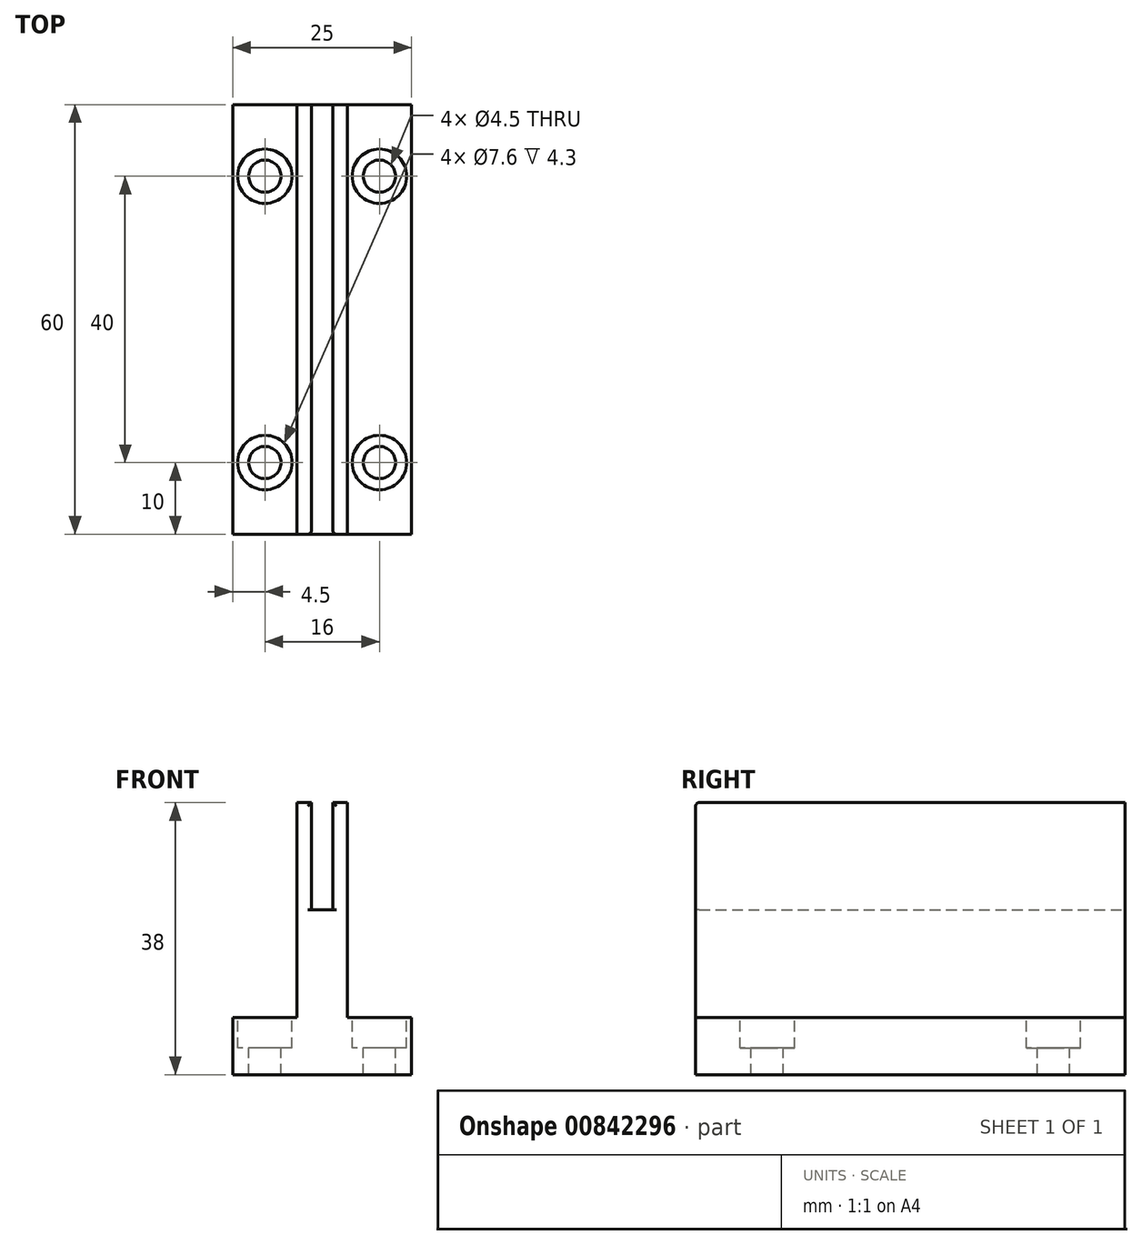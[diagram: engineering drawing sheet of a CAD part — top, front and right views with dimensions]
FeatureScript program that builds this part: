
annotation { "Feature Type Name" : "Feature", "Feature Type Description" : "" }
export const myFeature = defineFeature(function(context is Context, id is Id, definition is map)
    precondition{}
    {
        {
            var Q0;
            Q0=qCreatedBy(makeId("Front.planeOp"),FACE);
            var sketch = newSketch(context, id + "F0", { "sketchPlane" : qUnion([Q0])});
            skLineSegment(sketch, "E0", {"start": v(0, 17.87) * mm, "end": v(-1.5, 17.87) * mm});
            skLineSegment(sketch, "E1", {"start": v(-1.5, 17.87) * mm, "end": v(-1.5, 32.87) * mm});
            skLineSegment(sketch, "E2", {"start": v(-1.5, 32.87) * mm, "end": v(-3.5, 32.87) * mm});
            skLineSegment(sketch, "E3", {"start": v(-3.5, 32.87) * mm, "end": v(-3.5, 2.87) * mm});
            skLineSegment(sketch, "E4", {"start": v(-3.5, 2.87) * mm, "end": v(-12.5, 2.87) * mm});
            skLineSegment(sketch, "E5", {"start": v(-12.5, 2.87) * mm, "end": v(-12.5, -5.13) * mm});
            skLineSegment(sketch, "E6", {"start": v(-12.5, -5.13) * mm, "end": v(0, -5.13) * mm});
            skLineSegment(sketch, "E7", {"start": v(0, -5.13) * mm, "end": v(0, 17.87) * mm});
            skLineSegment(sketch, "E8.MirrorCS", {"start": v(1.5, 32.87) * mm, "end": v(3.5, 32.87) * mm});
            skLineSegment(sketch, "E9.MirrorCS", {"start": v(3.5, 32.87) * mm, "end": v(3.5, 2.87) * mm});
            skLineSegment(sketch, "E10.MirrorCS", {"start": v(3.5, 2.87) * mm, "end": v(12.5, 2.87) * mm});
            skLineSegment(sketch, "E11.MirrorCS", {"start": v(1.5, 17.87) * mm, "end": v(1.5, 32.87) * mm});
            skLineSegment(sketch, "E12.MirrorCS", {"start": v(12.5, 2.87) * mm, "end": v(12.5, -5.13) * mm});
            skLineSegment(sketch, "E13.MirrorCS", {"start": v(12.5, -5.13) * mm, "end": v(0, -5.13) * mm});
            skLineSegment(sketch, "E14.MirrorCS", {"start": v(0, 17.87) * mm, "end": v(1.5, 17.87) * mm});
            skSolve(sketch);
        }
        {
            var Q0;
            Q0=makeQuery(id+"F0.imprint","IMPRINT",FACE,{"disambiguationData":[TD([[makeQuery(id+"F0.imprint","IMPRINT",EDGE,{"derivedFrom":sQuery(id+"F0.wireOp",EDGE,"E0")}),1.0]])]});
            var Q1;
            Q1=makeQuery(id+"F0.imprint","IMPRINT",FACE,{"disambiguationData":[TD([[makeQuery(id+"F0.imprint","IMPRINT",EDGE,{"derivedFrom":sQuery(id+"F0.wireOp",EDGE,"E7")}),-1.0]])]});
            extrude(context, id + "F1", {"entities" : qUnion([Q0, Q1]), "depth" : 60 * mm, "offsetDistance" : 25 * mm});
        }
        {
            var Q0;
            Q0=makeQuery(id+"F1.opExtrude","SWEPT_FACE",FACE,{"disambiguationData":[OSD([sQuery(id+"F0.wireOp",EDGE,"E10.MirrorCS")])]});
            var sketch = newSketch(context, id + "F2", { "sketchPlane" : qUnion([Q0])});
            skCircle(sketch, "E15", {"center": v(8, -50) * mm, "radius": 1.96 * mm});
            skCircle(sketch, "E16", {"center": v(8, -50) * mm, "radius": 1.9 * mm});
            skCircle(sketch, "E17", {"center": v(8, -10) * mm, "radius": 2.01 * mm});
            skCircle(sketch, "E18", {"center": v(-8, -50) * mm, "radius": 2.05 * mm});
            skCircle(sketch, "E19", {"center": v(-8, -10) * mm, "radius": 2.04 * mm});
            skSolve(sketch);
        }
        {
            var Q0;
            Q0=sQuery(id+"F2.wireOp",VERTEX,"E18.center");
            var Q1;
            Q1=sQuery(id+"F2.wireOp",VERTEX,"E19.center");
            var Q2;
            Q2=sQuery(id+"F2.wireOp",VERTEX,"E15.center");
            var Q3;
            Q3=sQuery(id+"F2.wireOp",VERTEX,"E17.center");
            var Q4;
            Q4=makeQuery(id+"F1.opExtrude","SWEPT_BODY",BODY,{"disambiguationData":[OSD([sQuery(id+"F0.wireOp",EDGE,"E0"),sQuery(id+"F0.wireOp",EDGE,"E1"),sQuery(id+"F0.wireOp",EDGE,"E2"),sQuery(id+"F0.wireOp",EDGE,"E3"),sQuery(id+"F0.wireOp",EDGE,"E4"),sQuery(id+"F0.wireOp",EDGE,"E5"),sQuery(id+"F0.wireOp",EDGE,"E6"),sQuery(id+"F0.wireOp",EDGE,"E8.MirrorCS"),sQuery(id+"F0.wireOp",EDGE,"E9.MirrorCS"),sQuery(id+"F0.wireOp",EDGE,"E10.MirrorCS"),sQuery(id+"F0.wireOp",EDGE,"E11.MirrorCS"),sQuery(id+"F0.wireOp",EDGE,"E12.MirrorCS"),sQuery(id+"F0.wireOp",EDGE,"E13.MirrorCS"),sQuery(id+"F0.wireOp",EDGE,"E14.MirrorCS")])]});
            hole(context, id + "F3", {"style" : HoleStyle.C_BORE, "endStyle" : HoleEndStyle.THROUGH, "holeDiameter" : 4.5 * mm, "cBoreDiameter" : 7.6 * mm, "cBoreDepth" : 4.3 * mm, "majorDiameter" : 5 * mm, "isTappedThrough" : true, "tappedDepth" : 12 * mm, "tapClearance" : 3, "startFromSketch" : true, "locations" : qUnion([Q0, Q1, Q2, Q3]), "scope" : qUnion([Q4])});
        }
        {
            var Q0;
            Q0=makeQuery(id+"F1.opExtrude","CAP_EDGE",EDGE,{"disambiguationData":[OSD([sQuery(id+"F0.wireOp",EDGE,"E1")])],"isStart":false});
            var Q1;
            Q1=makeQuery(id+"F1.opExtrude","CAP_EDGE",EDGE,{"disambiguationData":[OSD([sQuery(id+"F0.wireOp",EDGE,"E11.MirrorCS")])],"isStart":false});
            var Q2;
            Q2=makeQuery(id+"F1.opExtrude","CAP_EDGE",EDGE,{"disambiguationData":[OSD([sQuery(id+"F0.wireOp",EDGE,"E8.MirrorCS")])],"isStart":false});
            var Q3;
            Q3=makeQuery(id+"F1.opExtrude","CAP_EDGE",EDGE,{"disambiguationData":[OSD([sQuery(id+"F0.wireOp",EDGE,"E2")])],"isStart":false});
            fillet(context, id + "F4", {"entities" : qUnion([Q0, Q1, Q2, Q3]), "radius" : 0.5 * mm, "tangentPropagation" : true, "allowEdgeOverflow" : false});
        }
    });
